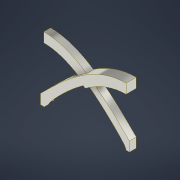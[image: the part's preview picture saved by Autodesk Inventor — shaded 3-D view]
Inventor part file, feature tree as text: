
AUTODESK INVENTOR PART (.ipt)
format: ipt  version: 2022 (Build 260153000, 153)  size: 403,968 bytes
history: native  units: in
note: dims shown in document units (in); Inventor stores cm internally (conversion verified against a paired STEP export)
features: sketch x4, other x4, extrude x3, plane x2, projected_geometry x2, revolve x1
ambient origin geometry x8: Origin, YZ Plane, XZ Plane, XY Plane, X Axis, Y Axis, Z Axis, Center Point
bodies: Body1 (feature_tree)
feature tree (16):
  sketch  "Sketch1"  dims[d4=0.0in d5=90.0deg d6=0.0in d7=90.0deg]
  extrude  "Extrusion3"  TaperAngle=0.0deg  [1 undecoded]
  extrude  "Extrusion4"  Depth=0.125in
  plane  "Work Plane1"
  revolve  "Revolution1"  [1 undecoded]
  extrude  "Extrusion5"  Depth=0.125in TaperAngle=0.0deg
  plane  "Work Plane2"
  sketch  "Sketch4"  dims[d16=0.1875in d17=0.0in d18=0.125in d19=0.0in d28=0.0in d29=180.0deg d30=0.0in d31=180.0deg d32=90.0deg d33=5.0in d34=0.0in]
  other  "2D Equation Curve1"
  other  "2D Equation Curve2"
  sketch  "Sketch2"  dims[d8=0.125in d9=0.125in]
  other  "2D Equation Curve3"
  other  "2D Equation Curve4"
  sketch  "Sketch3"  dims[d14=0.05in d15=0.05in]
  projected_geometry  "Projected Loop1"
  projected_geometry  "Projected Loop2"
note: 2 required parameter values undecoded (feature->parameter linkage not recoverable at this tier; creation-order binding heuristic only, values carry confidence <= 0.55)